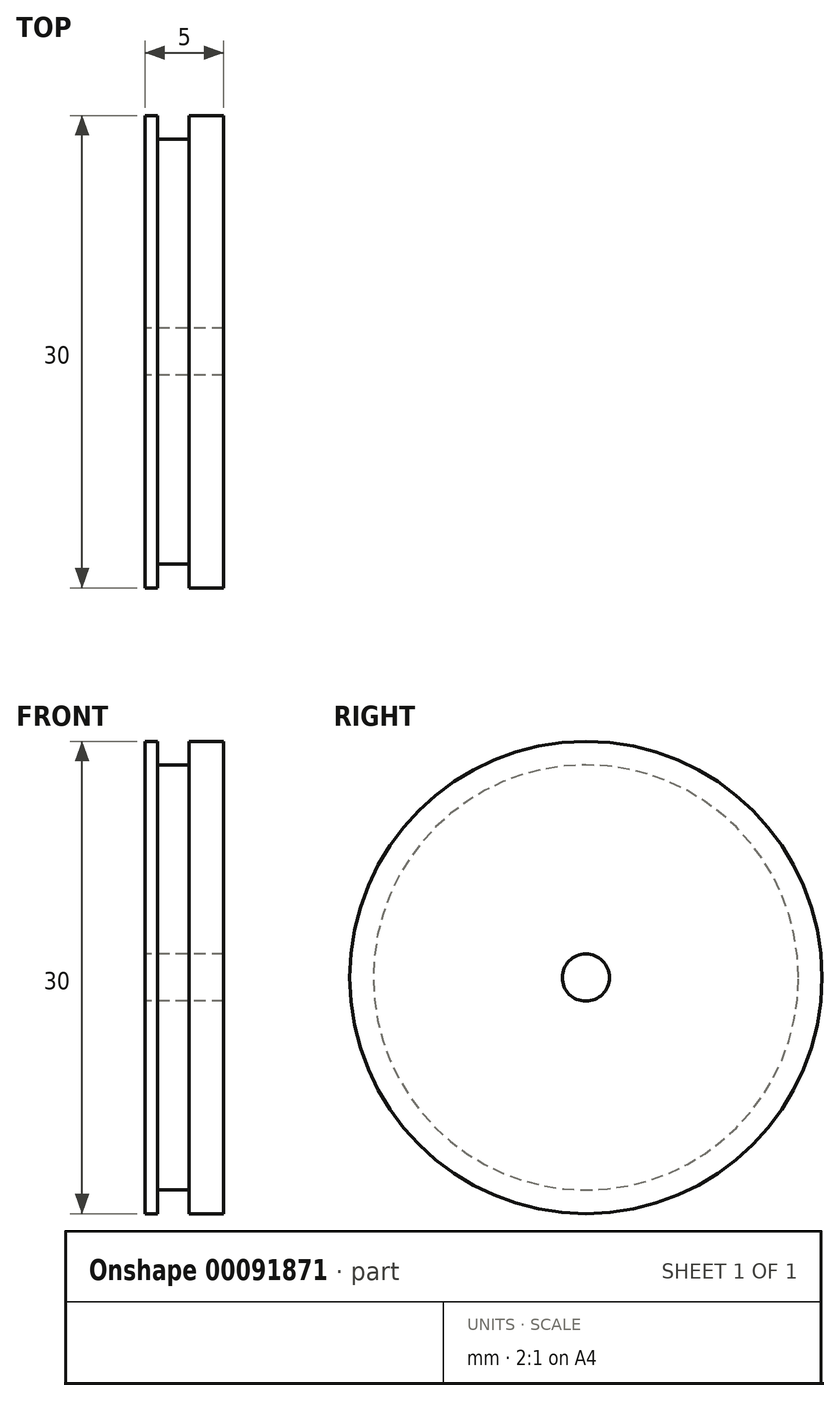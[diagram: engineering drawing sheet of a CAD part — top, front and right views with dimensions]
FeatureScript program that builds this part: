
annotation { "Feature Type Name" : "Feature", "Feature Type Description" : "" }
export const myFeature = defineFeature(function(context is Context, id is Id, definition is map)
    precondition{}
    {
        {
            var Q0;
            Q0=qCreatedBy(makeId("Front.planeOp"),FACE);
            var sketch = newSketch(context, id + "F0", { "sketchPlane" : qUnion([Q0])});
            skLineSegment(sketch, "E0.bottom", {"start": v(-2.5, 2.5) * mm, "end": v(-1.72, 2.5) * mm});
            skLineSegment(sketch, "E0.top", {"start": v(-2.5, -2.5) * mm, "end": v(2.5, -2.5) * mm});
            skLineSegment(sketch, "E0.left", {"start": v(-2.5, 2.5) * mm, "end": v(-2.5, -2.5) * mm});
            skLineSegment(sketch, "E0.right", {"start": v(2.5, 2.5) * mm, "end": v(2.5, -2.5) * mm});
            skPoint(sketch, "E0.middle", {"position": v(0, 0) * mm});
            skLineSegment(sketch, "E1.top", {"start": v(-1.72, 1) * mm, "end": v(0.28, 1) * mm});
            skLineSegment(sketch, "E1.left", {"start": v(-1.72, 2.5) * mm, "end": v(-1.72, 1) * mm});
            skLineSegment(sketch, "E1.right", {"start": v(0.28, 2.5) * mm, "end": v(0.28, 1) * mm});
            skLineSegment(sketch, "E2", {"start": v(-2.5, 2.5) * mm, "end": v(-2.5, -11) * mm});
            skLineSegment(sketch, "E3", {"start": v(2.5, -11) * mm, "end": v(2.5, -2.5) * mm});
            skLineSegment(sketch, "E4.trimOffspring", {"start": v(0.28, 2.5) * mm, "end": v(2.5, 2.5) * mm});
            skLineSegment(sketch, "E5", {"start": v(4.4, -12.5) * mm, "end": v(8.62, -12.5) * mm});
            skLineSegment(sketch, "E6", {"start": v(3.57, -12.5) * mm, "end": v(3.57, -11) * mm});
            skLineSegment(sketch, "E7", {"start": v(2.5, -11) * mm, "end": v(-2.5, -11) * mm});
            skPoint(sketch, "E8.orphan", {"position": v(2.5, -12.5) * mm});
            skSolve(sketch);
        }
        {
            var Q0;
            Q0 = qSketchRegion(id + "F0", true);
            var Q1;
            Q1=sQuery(id+"F0.wireOp",EDGE,"E5");
            revolve(context, id + "F1", {"entities" : qUnion([Q0]), "axis" : qUnion([Q1]), "revolveType" : RevolveType.FULL});
        }
    });
